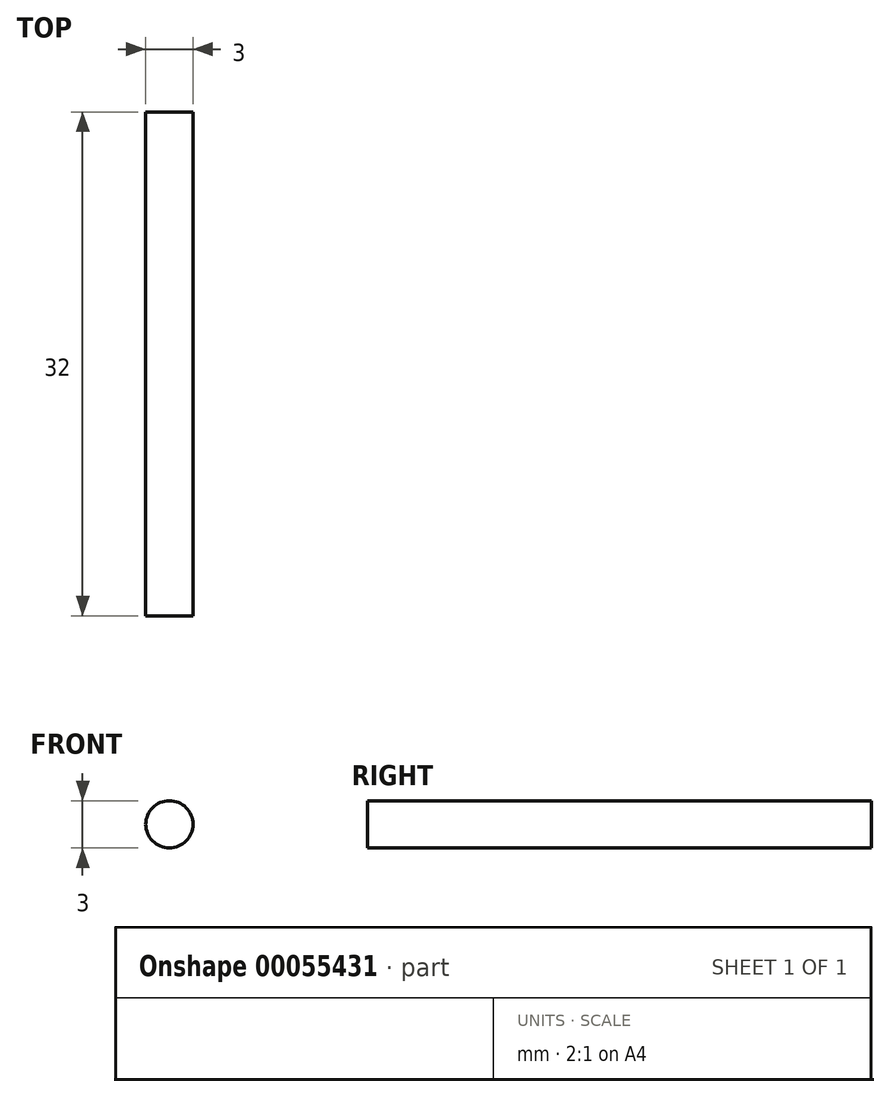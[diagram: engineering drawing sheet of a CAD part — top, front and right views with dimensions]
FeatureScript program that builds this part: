
annotation { "Feature Type Name" : "Feature", "Feature Type Description" : "" }
export const myFeature = defineFeature(function(context is Context, id is Id, definition is map)
    precondition{}
    {
        {
            var Q0;
            Q0=qCreatedBy(makeId("Front.planeOp"),FACE);
            var sketch = newSketch(context, id + "F0", { "sketchPlane" : qUnion([Q0])});
            skCircle(sketch, "E0", {"center": v(-0.22, 0) * mm, "radius": 1.5 * mm});
            skSolve(sketch);
        }
        {
            var Q0;
            Q0 = qSketchRegion(id + "F0", true);
            extrude(context, id + "F1", {"entities" : qUnion([Q0]), "depth" : 32 * mm});
        }
    });
